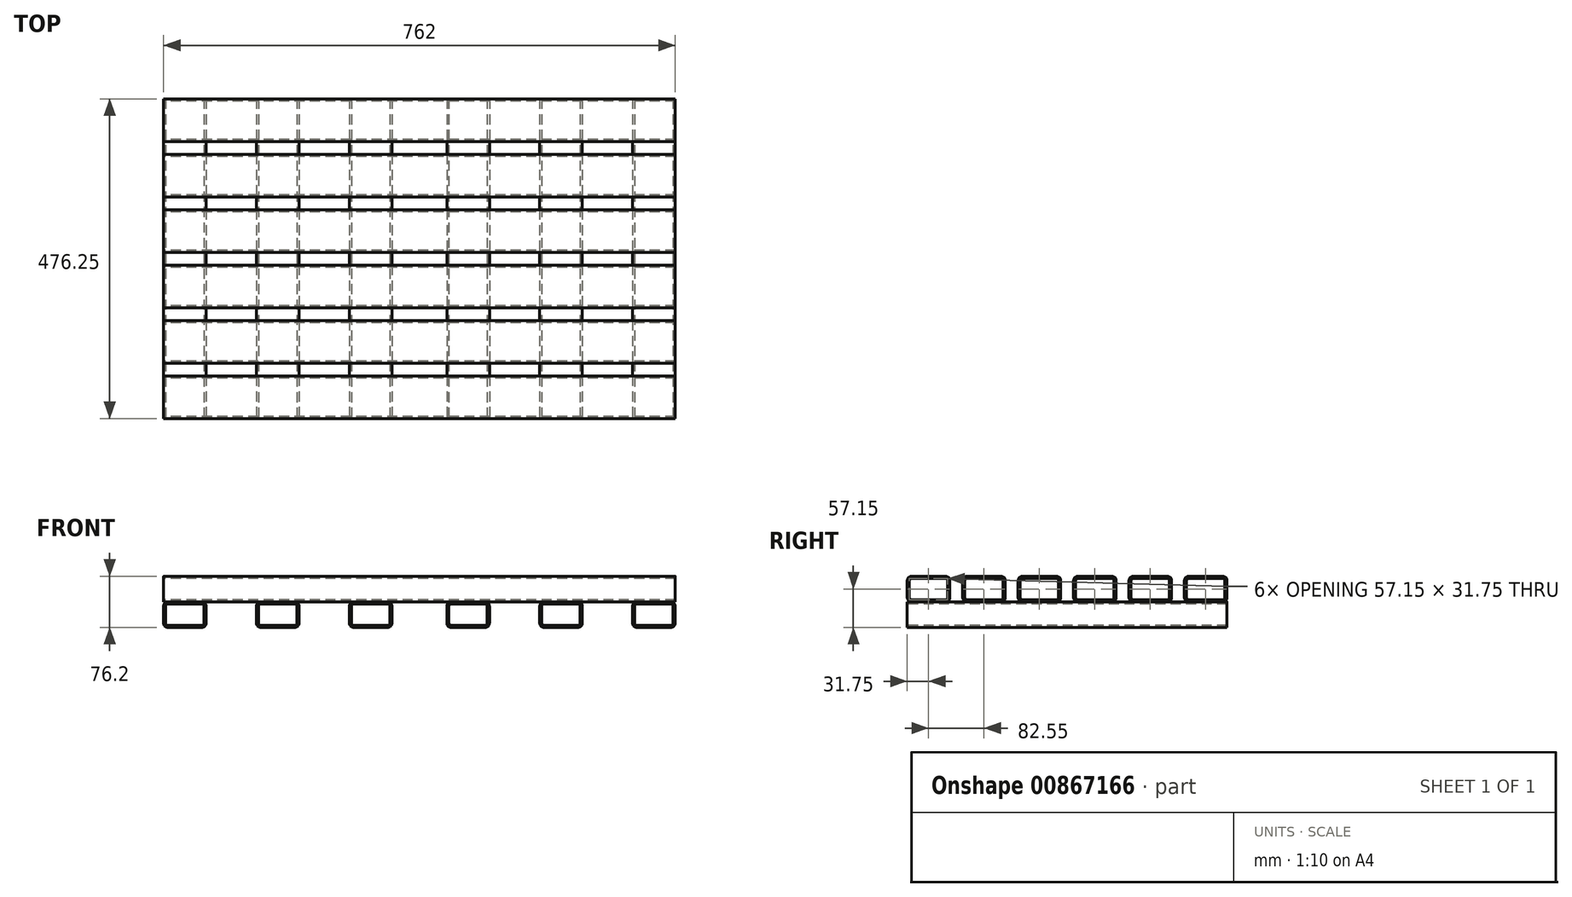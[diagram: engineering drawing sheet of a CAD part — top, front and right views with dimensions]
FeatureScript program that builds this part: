
annotation { "Feature Type Name" : "Feature", "Feature Type Description" : "" }
export const myFeature = defineFeature(function(context is Context, id is Id, definition is map)
    precondition{}
    {
        {
            var Q0;
            Q0=qCreatedBy(makeId("Right.planeOp"),FACE);
            var sketch = newSketch(context, id + "F0", { "sketchPlane" : qUnion([Q0])});
            skLineSegment(sketch, "E0.bottom", {"start": v(6.35, 0) * mm, "end": v(57.15, 0) * mm});
            skLineSegment(sketch, "E0.top", {"start": v(6.35, -38.1) * mm, "end": v(57.15, -38.1) * mm});
            skLineSegment(sketch, "E0.left", {"start": v(0, -6.35) * mm, "end": v(0, -31.75) * mm});
            skLineSegment(sketch, "E0.right", {"start": v(63.5, -6.35) * mm, "end": v(63.5, -31.75) * mm});
            skPoint(sketch, "E1.visualSharp", {"position": v(0, 0) * mm});
            skArc(sketch, "E1.filletArc", {"start": v(6.35, 0) * mm, "mid": v(1.86, -1.86) * mm, "end": v(0, -6.35) * mm});
            skPoint(sketch, "E2.visualSharp", {"position": v(0, -38.1) * mm});
            skArc(sketch, "E2.filletArc", {"start": v(0, -31.75) * mm, "mid": v(1.86, -36.24) * mm, "end": v(6.35, -38.1) * mm});
            skPoint(sketch, "E3.visualSharp", {"position": v(63.5, 0) * mm});
            skArc(sketch, "E3.filletArc", {"start": v(63.5, -6.35) * mm, "mid": v(61.64, -1.86) * mm, "end": v(57.15, 0) * mm});
            skPoint(sketch, "E4.visualSharp", {"position": v(63.5, -38.1) * mm});
            skArc(sketch, "E4.filletArc", {"start": v(57.15, -38.1) * mm, "mid": v(61.64, -36.24) * mm, "end": v(63.5, -31.75) * mm});
            skLineSegment(sketch, "E5.0", {"start": v(6.35, -3.18) * mm, "end": v(57.15, -3.18) * mm});
            skArc(sketch, "E5.1", {"start": v(60.33, -6.35) * mm, "mid": v(59.4, -4.1) * mm, "end": v(57.15, -3.17) * mm});
            skArc(sketch, "E5.2", {"start": v(6.35, -3.17) * mm, "mid": v(4.1, -4.1) * mm, "end": v(3.17, -6.35) * mm});
            skLineSegment(sketch, "E5.3", {"start": v(60.33, -6.35) * mm, "end": v(60.33, -31.75) * mm});
            skLineSegment(sketch, "E5.4", {"start": v(3.18, -6.35) * mm, "end": v(3.18, -31.75) * mm});
            skArc(sketch, "E5.5", {"start": v(3.18, -31.75) * mm, "mid": v(4.1, -34) * mm, "end": v(6.35, -34.92) * mm});
            skLineSegment(sketch, "E5.6", {"start": v(6.35, -34.92) * mm, "end": v(57.15, -34.92) * mm});
            skArc(sketch, "E5.7", {"start": v(57.15, -34.92) * mm, "mid": v(59.4, -34) * mm, "end": v(60.33, -31.75) * mm});
            skArc(sketch, "E6.1.0.0", {"start": v(88.9, 0) * mm, "mid": v(84.4, -1.86) * mm, "end": v(82.55, -6.35) * mm});
            skLineSegment(sketch, "E6.1.0.1", {"start": v(88.9, 0) * mm, "end": v(139.7, 0) * mm});
            skArc(sketch, "E6.1.0.2", {"start": v(146.05, -6.35) * mm, "mid": v(144.2, -1.86) * mm, "end": v(139.7, 0) * mm});
            skLineSegment(sketch, "E6.1.0.3", {"start": v(146.05, -6.35) * mm, "end": v(146.05, -31.75) * mm});
            skArc(sketch, "E6.1.0.4", {"start": v(139.7, -38.1) * mm, "mid": v(144.2, -36.24) * mm, "end": v(146.05, -31.75) * mm});
            skLineSegment(sketch, "E6.1.0.5", {"start": v(88.9, -38.1) * mm, "end": v(139.7, -38.1) * mm});
            skArc(sketch, "E6.1.0.6", {"start": v(82.55, -31.75) * mm, "mid": v(84.4, -36.24) * mm, "end": v(88.9, -38.1) * mm});
            skLineSegment(sketch, "E6.1.0.7", {"start": v(82.55, -6.35) * mm, "end": v(82.55, -31.75) * mm});
            skArc(sketch, "E6.1.0.8", {"start": v(88.9, -3.17) * mm, "mid": v(86.65, -4.1) * mm, "end": v(85.72, -6.35) * mm});
            skLineSegment(sketch, "E6.1.0.9", {"start": v(88.9, -3.18) * mm, "end": v(139.7, -3.18) * mm});
            skArc(sketch, "E6.1.0.10", {"start": v(142.88, -6.35) * mm, "mid": v(141.95, -4.1) * mm, "end": v(139.7, -3.17) * mm});
            skLineSegment(sketch, "E6.1.0.11", {"start": v(142.88, -6.35) * mm, "end": v(142.88, -31.75) * mm});
            skArc(sketch, "E6.1.0.12", {"start": v(139.7, -34.92) * mm, "mid": v(141.95, -34) * mm, "end": v(142.88, -31.75) * mm});
            skLineSegment(sketch, "E6.1.0.13", {"start": v(88.9, -34.92) * mm, "end": v(139.7, -34.92) * mm});
            skArc(sketch, "E6.1.0.14", {"start": v(85.73, -31.75) * mm, "mid": v(86.65, -34) * mm, "end": v(88.9, -34.92) * mm});
            skLineSegment(sketch, "E6.1.0.15", {"start": v(85.72, -6.35) * mm, "end": v(85.72, -31.75) * mm});
            skArc(sketch, "E6.2.0.0", {"start": v(171.45, 0) * mm, "mid": v(166.96, -1.86) * mm, "end": v(165.1, -6.35) * mm});
            skLineSegment(sketch, "E6.2.0.1", {"start": v(171.45, 0) * mm, "end": v(222.25, 0) * mm});
            skArc(sketch, "E6.2.0.2", {"start": v(228.6, -6.35) * mm, "mid": v(226.74, -1.86) * mm, "end": v(222.25, 0) * mm});
            skLineSegment(sketch, "E6.2.0.3", {"start": v(228.6, -6.35) * mm, "end": v(228.6, -31.75) * mm});
            skArc(sketch, "E6.2.0.4", {"start": v(222.25, -38.1) * mm, "mid": v(226.74, -36.24) * mm, "end": v(228.6, -31.75) * mm});
            skLineSegment(sketch, "E6.2.0.5", {"start": v(171.45, -38.1) * mm, "end": v(222.25, -38.1) * mm});
            skArc(sketch, "E6.2.0.6", {"start": v(165.1, -31.75) * mm, "mid": v(166.96, -36.24) * mm, "end": v(171.45, -38.1) * mm});
            skLineSegment(sketch, "E6.2.0.7", {"start": v(165.1, -6.35) * mm, "end": v(165.1, -31.75) * mm});
            skArc(sketch, "E6.2.0.8", {"start": v(171.45, -3.17) * mm, "mid": v(169.2, -4.1) * mm, "end": v(168.27, -6.35) * mm});
            skLineSegment(sketch, "E6.2.0.9", {"start": v(171.45, -3.18) * mm, "end": v(222.25, -3.18) * mm});
            skArc(sketch, "E6.2.0.10", {"start": v(225.43, -6.35) * mm, "mid": v(224.5, -4.1) * mm, "end": v(222.25, -3.17) * mm});
            skLineSegment(sketch, "E6.2.0.11", {"start": v(225.43, -6.35) * mm, "end": v(225.43, -31.75) * mm});
            skArc(sketch, "E6.2.0.12", {"start": v(222.25, -34.92) * mm, "mid": v(224.5, -34) * mm, "end": v(225.43, -31.75) * mm});
            skLineSegment(sketch, "E6.2.0.13", {"start": v(171.45, -34.92) * mm, "end": v(222.25, -34.92) * mm});
            skArc(sketch, "E6.2.0.14", {"start": v(168.27, -31.75) * mm, "mid": v(169.2, -34) * mm, "end": v(171.45, -34.92) * mm});
            skLineSegment(sketch, "E6.2.0.15", {"start": v(168.28, -6.35) * mm, "end": v(168.28, -31.75) * mm});
            skLineSegment(sketch, "E6.direction1", {"start": v(0, -6.35) * mm, "end": v(82.55, -6.35) * mm, "construction": true});
            skArc(sketch, "E7.0.3.0", {"start": v(254, 0) * mm, "mid": v(249.5, -1.86) * mm, "end": v(247.65, -6.35) * mm});
            skLineSegment(sketch, "E7.4.3.0", {"start": v(254, 0) * mm, "end": v(304.8, 0) * mm});
            skArc(sketch, "E7.7.3.0", {"start": v(311.15, -6.35) * mm, "mid": v(309.3, -1.86) * mm, "end": v(304.8, 0) * mm});
            skLineSegment(sketch, "E7.11.3.0", {"start": v(311.15, -6.35) * mm, "end": v(311.15, -31.75) * mm});
            skArc(sketch, "E7.14.3.0", {"start": v(304.8, -38.1) * mm, "mid": v(309.3, -36.24) * mm, "end": v(311.15, -31.75) * mm});
            skLineSegment(sketch, "E7.18.3.0", {"start": v(254, -38.1) * mm, "end": v(304.8, -38.1) * mm});
            skArc(sketch, "E7.21.3.0", {"start": v(247.65, -31.75) * mm, "mid": v(249.5, -36.24) * mm, "end": v(254, -38.1) * mm});
            skLineSegment(sketch, "E7.25.3.0", {"start": v(247.65, -6.35) * mm, "end": v(247.65, -31.75) * mm});
            skArc(sketch, "E7.28.3.0", {"start": v(254, -3.17) * mm, "mid": v(251.75, -4.1) * mm, "end": v(250.83, -6.35) * mm});
            skLineSegment(sketch, "E7.32.3.0", {"start": v(254, -3.18) * mm, "end": v(304.8, -3.18) * mm});
            skArc(sketch, "E7.35.3.0", {"start": v(307.97, -6.35) * mm, "mid": v(307.05, -4.1) * mm, "end": v(304.8, -3.17) * mm});
            skLineSegment(sketch, "E7.39.3.0", {"start": v(307.98, -6.35) * mm, "end": v(307.98, -31.75) * mm});
            skArc(sketch, "E7.42.3.0", {"start": v(304.8, -34.92) * mm, "mid": v(307.05, -34) * mm, "end": v(307.97, -31.75) * mm});
            skLineSegment(sketch, "E7.46.3.0", {"start": v(254, -34.92) * mm, "end": v(304.8, -34.92) * mm});
            skArc(sketch, "E7.49.3.0", {"start": v(250.83, -31.75) * mm, "mid": v(251.75, -34) * mm, "end": v(254, -34.92) * mm});
            skLineSegment(sketch, "E7.53.3.0", {"start": v(250.82, -6.35) * mm, "end": v(250.82, -31.75) * mm});
            skArc(sketch, "E8.0.4.0", {"start": v(336.55, 0) * mm, "mid": v(332.06, -1.86) * mm, "end": v(330.2, -6.35) * mm});
            skLineSegment(sketch, "E8.4.4.0", {"start": v(336.55, 0) * mm, "end": v(387.35, 0) * mm});
            skArc(sketch, "E8.7.4.0", {"start": v(393.7, -6.35) * mm, "mid": v(391.84, -1.86) * mm, "end": v(387.35, 0) * mm});
            skLineSegment(sketch, "E8.11.4.0", {"start": v(393.7, -6.35) * mm, "end": v(393.7, -31.75) * mm});
            skArc(sketch, "E8.14.4.0", {"start": v(387.35, -38.1) * mm, "mid": v(391.84, -36.24) * mm, "end": v(393.7, -31.75) * mm});
            skLineSegment(sketch, "E8.18.4.0", {"start": v(336.55, -38.1) * mm, "end": v(387.35, -38.1) * mm});
            skArc(sketch, "E8.21.4.0", {"start": v(330.2, -31.75) * mm, "mid": v(332.06, -36.24) * mm, "end": v(336.55, -38.1) * mm});
            skLineSegment(sketch, "E8.25.4.0", {"start": v(330.2, -6.35) * mm, "end": v(330.2, -31.75) * mm});
            skArc(sketch, "E8.28.4.0", {"start": v(336.55, -3.17) * mm, "mid": v(334.3, -4.1) * mm, "end": v(333.38, -6.35) * mm});
            skLineSegment(sketch, "E8.32.4.0", {"start": v(336.55, -3.18) * mm, "end": v(387.35, -3.18) * mm});
            skArc(sketch, "E8.35.4.0", {"start": v(390.52, -6.35) * mm, "mid": v(389.6, -4.1) * mm, "end": v(387.35, -3.17) * mm});
            skLineSegment(sketch, "E8.39.4.0", {"start": v(390.53, -6.35) * mm, "end": v(390.53, -31.75) * mm});
            skArc(sketch, "E8.42.4.0", {"start": v(387.35, -34.92) * mm, "mid": v(389.6, -34) * mm, "end": v(390.52, -31.75) * mm});
            skLineSegment(sketch, "E8.46.4.0", {"start": v(336.55, -34.92) * mm, "end": v(387.35, -34.92) * mm});
            skArc(sketch, "E8.49.4.0", {"start": v(333.38, -31.75) * mm, "mid": v(334.3, -34) * mm, "end": v(336.55, -34.92) * mm});
            skLineSegment(sketch, "E8.53.4.0", {"start": v(333.38, -6.35) * mm, "end": v(333.38, -31.75) * mm});
            skArc(sketch, "E8.0.5.0", {"start": v(419.1, 0) * mm, "mid": v(414.6, -1.86) * mm, "end": v(412.75, -6.35) * mm});
            skLineSegment(sketch, "E8.4.5.0", {"start": v(419.1, 0) * mm, "end": v(469.9, 0) * mm});
            skArc(sketch, "E8.7.5.0", {"start": v(476.25, -6.35) * mm, "mid": v(474.4, -1.86) * mm, "end": v(469.9, 0) * mm});
            skLineSegment(sketch, "E8.11.5.0", {"start": v(476.25, -6.35) * mm, "end": v(476.25, -31.75) * mm});
            skArc(sketch, "E8.14.5.0", {"start": v(469.9, -38.1) * mm, "mid": v(474.4, -36.24) * mm, "end": v(476.25, -31.75) * mm});
            skLineSegment(sketch, "E8.18.5.0", {"start": v(419.1, -38.1) * mm, "end": v(469.9, -38.1) * mm});
            skArc(sketch, "E8.21.5.0", {"start": v(412.75, -31.75) * mm, "mid": v(414.6, -36.24) * mm, "end": v(419.1, -38.1) * mm});
            skLineSegment(sketch, "E8.25.5.0", {"start": v(412.75, -6.35) * mm, "end": v(412.75, -31.75) * mm});
            skArc(sketch, "E8.28.5.0", {"start": v(419.1, -3.17) * mm, "mid": v(416.85, -4.1) * mm, "end": v(415.93, -6.35) * mm});
            skLineSegment(sketch, "E8.32.5.0", {"start": v(419.1, -3.18) * mm, "end": v(469.9, -3.18) * mm});
            skArc(sketch, "E8.35.5.0", {"start": v(473.07, -6.35) * mm, "mid": v(472.15, -4.1) * mm, "end": v(469.9, -3.17) * mm});
            skLineSegment(sketch, "E8.39.5.0", {"start": v(473.08, -6.35) * mm, "end": v(473.08, -31.75) * mm});
            skArc(sketch, "E8.42.5.0", {"start": v(469.9, -34.92) * mm, "mid": v(472.15, -34) * mm, "end": v(473.07, -31.75) * mm});
            skLineSegment(sketch, "E8.46.5.0", {"start": v(419.1, -34.92) * mm, "end": v(469.9, -34.92) * mm});
            skArc(sketch, "E8.49.5.0", {"start": v(415.93, -31.75) * mm, "mid": v(416.85, -34) * mm, "end": v(419.1, -34.92) * mm});
            skLineSegment(sketch, "E8.53.5.0", {"start": v(415.93, -6.35) * mm, "end": v(415.93, -31.75) * mm});
            skSolve(sketch);
        }
        {
            var Q0;
            Q0 = qSketchRegion(id + "F0", true);
            extrude(context, id + "F1", {"entities" : qUnion([Q0]), "endBound" : BoundingType.SYMMETRIC, "depth" : 762 * mm, "offsetDistance" : 25.4 * mm});
        }
        {
            var Q0;
            Q0=qCreatedBy(makeId("Front.planeOp"),FACE);
            var sketch = newSketch(context, id + "F2", { "sketchPlane" : qUnion([Q0])});
            skLineSegment(sketch, "E9.bottom", {"start": v(-236.32, -38.1) * mm, "end": v(-185.52, -38.1) * mm});
            skLineSegment(sketch, "E9.top", {"start": v(-236.32, -76.2) * mm, "end": v(-185.52, -76.2) * mm});
            skLineSegment(sketch, "E9.left", {"start": v(-242.67, -44.45) * mm, "end": v(-242.67, -69.85) * mm});
            skLineSegment(sketch, "E9.right", {"start": v(-179.17, -44.45) * mm, "end": v(-179.17, -69.85) * mm});
            skPoint(sketch, "E10.visualSharp", {"position": v(-242.67, -38.1) * mm});
            skArc(sketch, "E10.filletArc", {"start": v(-236.32, -38.1) * mm, "mid": v(-240.81, -39.96) * mm, "end": v(-242.67, -44.45) * mm});
            skPoint(sketch, "E11.visualSharp", {"position": v(-242.67, -76.2) * mm});
            skArc(sketch, "E11.filletArc", {"start": v(-242.67, -69.85) * mm, "mid": v(-240.81, -74.34) * mm, "end": v(-236.32, -76.2) * mm});
            skPoint(sketch, "E12.visualSharp", {"position": v(-179.17, -38.1) * mm});
            skArc(sketch, "E12.filletArc", {"start": v(-179.17, -44.45) * mm, "mid": v(-181.03, -39.96) * mm, "end": v(-185.52, -38.1) * mm});
            skPoint(sketch, "E13.visualSharp", {"position": v(-179.17, -76.2) * mm});
            skArc(sketch, "E13.filletArc", {"start": v(-185.52, -76.2) * mm, "mid": v(-181.03, -74.34) * mm, "end": v(-179.17, -69.85) * mm});
            skLineSegment(sketch, "E14.0", {"start": v(-236.32, -41.28) * mm, "end": v(-185.52, -41.28) * mm});
            skArc(sketch, "E14.1", {"start": v(-182.35, -44.45) * mm, "mid": v(-183.28, -42.2) * mm, "end": v(-185.52, -41.27) * mm});
            skArc(sketch, "E14.2", {"start": v(-236.32, -41.27) * mm, "mid": v(-238.57, -42.2) * mm, "end": v(-239.5, -44.45) * mm});
            skLineSegment(sketch, "E14.3", {"start": v(-182.35, -44.45) * mm, "end": v(-182.35, -69.85) * mm});
            skLineSegment(sketch, "E14.4", {"start": v(-239.5, -44.45) * mm, "end": v(-239.5, -69.85) * mm});
            skArc(sketch, "E14.5", {"start": v(-239.5, -69.85) * mm, "mid": v(-238.57, -72.1) * mm, "end": v(-236.32, -73.02) * mm});
            skLineSegment(sketch, "E14.6", {"start": v(-236.32, -73.02) * mm, "end": v(-185.52, -73.02) * mm});
            skArc(sketch, "E14.7", {"start": v(-185.52, -73.02) * mm, "mid": v(-183.28, -72.1) * mm, "end": v(-182.35, -69.85) * mm});
            skPoint(sketch, "E15", {"position": v(-210.92, -38.1) * mm});
            skLineSegment(sketch, "E16.bottom", {"start": v(185.52, -38.1) * mm, "end": v(236.32, -38.1) * mm});
            skLineSegment(sketch, "E16.top", {"start": v(185.52, -76.2) * mm, "end": v(236.32, -76.2) * mm});
            skLineSegment(sketch, "E16.left", {"start": v(179.17, -44.45) * mm, "end": v(179.17, -69.85) * mm});
            skLineSegment(sketch, "E16.right", {"start": v(242.67, -44.45) * mm, "end": v(242.67, -69.85) * mm});
            skPoint(sketch, "E17.visualSharp", {"position": v(179.17, -38.1) * mm});
            skArc(sketch, "E17.filletArc", {"start": v(185.52, -38.1) * mm, "mid": v(181.03, -39.96) * mm, "end": v(179.17, -44.45) * mm});
            skPoint(sketch, "E18.visualSharp", {"position": v(179.17, -76.2) * mm});
            skArc(sketch, "E18.filletArc", {"start": v(179.17, -69.85) * mm, "mid": v(181.03, -74.34) * mm, "end": v(185.52, -76.2) * mm});
            skPoint(sketch, "E19.visualSharp", {"position": v(242.67, -38.1) * mm});
            skArc(sketch, "E19.filletArc", {"start": v(242.67, -44.45) * mm, "mid": v(240.81, -39.96) * mm, "end": v(236.32, -38.1) * mm});
            skPoint(sketch, "E20.visualSharp", {"position": v(242.67, -76.2) * mm});
            skArc(sketch, "E20.filletArc", {"start": v(236.32, -76.2) * mm, "mid": v(240.81, -74.34) * mm, "end": v(242.67, -69.85) * mm});
            skLineSegment(sketch, "E21.0", {"start": v(185.52, -41.28) * mm, "end": v(236.32, -41.28) * mm});
            skArc(sketch, "E21.1", {"start": v(239.5, -44.45) * mm, "mid": v(238.57, -42.2) * mm, "end": v(236.32, -41.28) * mm});
            skArc(sketch, "E21.2", {"start": v(185.52, -41.28) * mm, "mid": v(183.28, -42.2) * mm, "end": v(182.35, -44.45) * mm});
            skLineSegment(sketch, "E21.3", {"start": v(239.5, -44.45) * mm, "end": v(239.5, -69.85) * mm});
            skLineSegment(sketch, "E21.4", {"start": v(182.35, -44.45) * mm, "end": v(182.35, -69.85) * mm});
            skArc(sketch, "E21.5", {"start": v(182.35, -69.85) * mm, "mid": v(183.28, -72.1) * mm, "end": v(185.52, -73.03) * mm});
            skLineSegment(sketch, "E21.6", {"start": v(185.52, -73.02) * mm, "end": v(236.32, -73.02) * mm});
            skArc(sketch, "E21.7", {"start": v(236.32, -73.03) * mm, "mid": v(238.57, -72.1) * mm, "end": v(239.5, -69.85) * mm});
            skPoint(sketch, "E22", {"position": v(210.92, -38.1) * mm});
            skLineSegment(sketch, "E23", {"start": v(-210.92, -38.1) * mm, "end": v(-210.92, 99.79) * mm, "construction": true});
            skSolve(sketch);
        }
        {
            var Q0;
            Q0=qCreatedBy(makeId("Front.planeOp"),FACE);
            var sketch = newSketch(context, id + "F3", { "sketchPlane" : qUnion([Q0])});
            skLineSegment(sketch, "E24.bottom", {"start": v(-374.65, -38.1) * mm, "end": v(-323.85, -38.1) * mm});
            skLineSegment(sketch, "E24.top", {"start": v(-374.65, -76.2) * mm, "end": v(-323.85, -76.2) * mm});
            skLineSegment(sketch, "E24.left", {"start": v(-381, -44.45) * mm, "end": v(-381, -69.85) * mm});
            skLineSegment(sketch, "E24.right", {"start": v(-317.5, -44.45) * mm, "end": v(-317.5, -69.85) * mm});
            skPoint(sketch, "E25.visualSharp", {"position": v(-381, -38.1) * mm});
            skArc(sketch, "E25.filletArc", {"start": v(-374.65, -38.1) * mm, "mid": v(-379.14, -39.96) * mm, "end": v(-381, -44.45) * mm});
            skPoint(sketch, "E26.visualSharp", {"position": v(-381, -76.2) * mm});
            skArc(sketch, "E26.filletArc", {"start": v(-381, -69.85) * mm, "mid": v(-379.14, -74.34) * mm, "end": v(-374.65, -76.2) * mm});
            skPoint(sketch, "E27.visualSharp", {"position": v(-317.5, -38.1) * mm});
            skArc(sketch, "E27.filletArc", {"start": v(-317.5, -44.45) * mm, "mid": v(-319.36, -39.96) * mm, "end": v(-323.85, -38.1) * mm});
            skPoint(sketch, "E28.visualSharp", {"position": v(-317.5, -76.2) * mm});
            skArc(sketch, "E28.filletArc", {"start": v(-323.85, -76.2) * mm, "mid": v(-319.36, -74.34) * mm, "end": v(-317.5, -69.85) * mm});
            skLineSegment(sketch, "E29.0", {"start": v(-374.65, -41.28) * mm, "end": v(-323.85, -41.28) * mm});
            skArc(sketch, "E29.1", {"start": v(-320.68, -44.45) * mm, "mid": v(-321.6, -42.2) * mm, "end": v(-323.85, -41.27) * mm});
            skArc(sketch, "E29.2", {"start": v(-374.65, -41.28) * mm, "mid": v(-376.9, -42.2) * mm, "end": v(-377.83, -44.45) * mm});
            skLineSegment(sketch, "E29.3", {"start": v(-320.68, -44.45) * mm, "end": v(-320.68, -69.85) * mm});
            skLineSegment(sketch, "E29.4", {"start": v(-377.83, -44.45) * mm, "end": v(-377.83, -69.85) * mm});
            skArc(sketch, "E29.5", {"start": v(-377.83, -69.85) * mm, "mid": v(-376.9, -72.1) * mm, "end": v(-374.65, -73.02) * mm});
            skLineSegment(sketch, "E29.6", {"start": v(-374.65, -73.02) * mm, "end": v(-323.85, -73.02) * mm});
            skArc(sketch, "E29.7", {"start": v(-323.85, -73.02) * mm, "mid": v(-321.6, -72.1) * mm, "end": v(-320.68, -69.85) * mm});
            skPoint(sketch, "E30", {"position": v(-349.25, -38.1) * mm});
            skLineSegment(sketch, "E31.bottom", {"start": v(-98, -38.1) * mm, "end": v(-47.2, -38.1) * mm});
            skLineSegment(sketch, "E31.top", {"start": v(-98, -76.2) * mm, "end": v(-47.2, -76.2) * mm});
            skLineSegment(sketch, "E31.left", {"start": v(-104.34, -44.45) * mm, "end": v(-104.34, -69.85) * mm});
            skLineSegment(sketch, "E31.right", {"start": v(-40.84, -44.45) * mm, "end": v(-40.84, -69.85) * mm});
            skPoint(sketch, "E32.visualSharp", {"position": v(-104.34, -38.1) * mm});
            skArc(sketch, "E32.filletArc", {"start": v(-98, -38.1) * mm, "mid": v(-102.48, -39.96) * mm, "end": v(-104.34, -44.45) * mm});
            skPoint(sketch, "E33.visualSharp", {"position": v(-104.34, -76.2) * mm});
            skArc(sketch, "E33.filletArc", {"start": v(-104.34, -69.85) * mm, "mid": v(-102.48, -74.34) * mm, "end": v(-98, -76.2) * mm});
            skPoint(sketch, "E34.visualSharp", {"position": v(-40.84, -38.1) * mm});
            skArc(sketch, "E34.filletArc", {"start": v(-40.84, -44.45) * mm, "mid": v(-42.7, -39.96) * mm, "end": v(-47.2, -38.1) * mm});
            skPoint(sketch, "E35.visualSharp", {"position": v(-40.84, -76.2) * mm});
            skArc(sketch, "E35.filletArc", {"start": v(-47.2, -76.2) * mm, "mid": v(-42.7, -74.34) * mm, "end": v(-40.84, -69.85) * mm});
            skLineSegment(sketch, "E36.0", {"start": v(-98, -41.28) * mm, "end": v(-47.2, -41.28) * mm});
            skArc(sketch, "E36.1", {"start": v(-44.02, -44.45) * mm, "mid": v(-44.95, -42.2) * mm, "end": v(-47.2, -41.27) * mm});
            skArc(sketch, "E36.2", {"start": v(-98, -41.28) * mm, "mid": v(-100.24, -42.2) * mm, "end": v(-101.17, -44.45) * mm});
            skLineSegment(sketch, "E36.3", {"start": v(-44.02, -44.45) * mm, "end": v(-44.02, -69.85) * mm});
            skLineSegment(sketch, "E36.4", {"start": v(-101.17, -44.45) * mm, "end": v(-101.17, -69.85) * mm});
            skArc(sketch, "E36.5", {"start": v(-101.17, -69.85) * mm, "mid": v(-100.24, -72.1) * mm, "end": v(-98, -73.03) * mm});
            skLineSegment(sketch, "E36.6", {"start": v(-98, -73.02) * mm, "end": v(-47.2, -73.02) * mm});
            skArc(sketch, "E36.7", {"start": v(-47.2, -73.02) * mm, "mid": v(-44.95, -72.1) * mm, "end": v(-44.02, -69.85) * mm});
            skPoint(sketch, "E37", {"position": v(-72.6, -38.1) * mm});
            skLineSegment(sketch, "E38.bottom", {"start": v(47.2, -38.1) * mm, "end": v(98, -38.1) * mm});
            skLineSegment(sketch, "E38.top", {"start": v(47.2, -76.2) * mm, "end": v(98, -76.2) * mm});
            skLineSegment(sketch, "E38.left", {"start": v(40.84, -44.45) * mm, "end": v(40.84, -69.85) * mm});
            skLineSegment(sketch, "E38.right", {"start": v(104.34, -44.45) * mm, "end": v(104.34, -69.85) * mm});
            skPoint(sketch, "E39.visualSharp", {"position": v(40.84, -38.1) * mm});
            skArc(sketch, "E39.filletArc", {"start": v(47.2, -38.1) * mm, "mid": v(42.7, -39.96) * mm, "end": v(40.84, -44.45) * mm});
            skPoint(sketch, "E40.visualSharp", {"position": v(40.84, -76.2) * mm});
            skArc(sketch, "E40.filletArc", {"start": v(40.84, -69.85) * mm, "mid": v(42.7, -74.34) * mm, "end": v(47.2, -76.2) * mm});
            skPoint(sketch, "E41.visualSharp", {"position": v(104.34, -38.1) * mm});
            skArc(sketch, "E41.filletArc", {"start": v(104.34, -44.45) * mm, "mid": v(102.48, -39.96) * mm, "end": v(98, -38.1) * mm});
            skPoint(sketch, "E42.visualSharp", {"position": v(104.34, -76.2) * mm});
            skArc(sketch, "E42.filletArc", {"start": v(98, -76.2) * mm, "mid": v(102.48, -74.34) * mm, "end": v(104.34, -69.85) * mm});
            skLineSegment(sketch, "E43.0", {"start": v(47.2, -41.27) * mm, "end": v(98, -41.27) * mm});
            skArc(sketch, "E43.1", {"start": v(101.17, -44.45) * mm, "mid": v(100.24, -42.2) * mm, "end": v(98, -41.27) * mm});
            skArc(sketch, "E43.2", {"start": v(47.2, -41.28) * mm, "mid": v(44.95, -42.2) * mm, "end": v(44.02, -44.45) * mm});
            skLineSegment(sketch, "E43.3", {"start": v(101.17, -44.45) * mm, "end": v(101.17, -69.85) * mm});
            skLineSegment(sketch, "E43.4", {"start": v(44.02, -44.45) * mm, "end": v(44.02, -69.85) * mm});
            skArc(sketch, "E43.5", {"start": v(44.02, -69.85) * mm, "mid": v(44.95, -72.1) * mm, "end": v(47.2, -73.03) * mm});
            skLineSegment(sketch, "E43.6", {"start": v(47.2, -73.02) * mm, "end": v(98, -73.02) * mm});
            skArc(sketch, "E43.7", {"start": v(98, -73.02) * mm, "mid": v(100.24, -72.1) * mm, "end": v(101.17, -69.85) * mm});
            skPoint(sketch, "E44", {"position": v(72.6, -38.1) * mm});
            skLineSegment(sketch, "E45.bottom", {"start": v(323.85, -38.1) * mm, "end": v(374.65, -38.1) * mm});
            skLineSegment(sketch, "E45.top", {"start": v(323.85, -76.2) * mm, "end": v(374.65, -76.2) * mm});
            skLineSegment(sketch, "E45.left", {"start": v(317.5, -44.45) * mm, "end": v(317.5, -69.85) * mm});
            skLineSegment(sketch, "E45.right", {"start": v(381, -44.45) * mm, "end": v(381, -69.85) * mm});
            skPoint(sketch, "E46.visualSharp", {"position": v(317.5, -38.1) * mm});
            skArc(sketch, "E46.filletArc", {"start": v(323.85, -38.1) * mm, "mid": v(319.36, -39.96) * mm, "end": v(317.5, -44.45) * mm});
            skPoint(sketch, "E47.visualSharp", {"position": v(317.5, -76.2) * mm});
            skArc(sketch, "E47.filletArc", {"start": v(317.5, -69.85) * mm, "mid": v(319.36, -74.34) * mm, "end": v(323.85, -76.2) * mm});
            skPoint(sketch, "E48.visualSharp", {"position": v(381, -38.1) * mm});
            skArc(sketch, "E48.filletArc", {"start": v(381, -44.45) * mm, "mid": v(379.14, -39.96) * mm, "end": v(374.65, -38.1) * mm});
            skPoint(sketch, "E49.visualSharp", {"position": v(381, -76.2) * mm});
            skArc(sketch, "E49.filletArc", {"start": v(374.65, -76.2) * mm, "mid": v(379.14, -74.34) * mm, "end": v(381, -69.85) * mm});
            skLineSegment(sketch, "E50.0", {"start": v(323.85, -41.28) * mm, "end": v(374.65, -41.28) * mm});
            skArc(sketch, "E50.1", {"start": v(377.83, -44.45) * mm, "mid": v(376.9, -42.2) * mm, "end": v(374.65, -41.28) * mm});
            skArc(sketch, "E50.2", {"start": v(323.85, -41.28) * mm, "mid": v(321.6, -42.2) * mm, "end": v(320.68, -44.45) * mm});
            skLineSegment(sketch, "E50.3", {"start": v(377.82, -44.45) * mm, "end": v(377.82, -69.85) * mm});
            skLineSegment(sketch, "E50.4", {"start": v(320.68, -44.45) * mm, "end": v(320.68, -69.85) * mm});
            skArc(sketch, "E50.5", {"start": v(320.68, -69.85) * mm, "mid": v(321.6, -72.1) * mm, "end": v(323.85, -73.03) * mm});
            skLineSegment(sketch, "E50.6", {"start": v(323.85, -73.02) * mm, "end": v(374.65, -73.02) * mm});
            skArc(sketch, "E50.7", {"start": v(374.65, -73.03) * mm, "mid": v(376.9, -72.1) * mm, "end": v(377.82, -69.85) * mm});
            skPoint(sketch, "E51", {"position": v(349.25, -38.1) * mm});
            skSolve(sketch);
        }
        {
            var Q0;
            Q0 = qSketchRegion(id + "F2", true);
            var Q1;
            Q1 = qSketchRegion(id + "F3", true);
            var Q2;
            Q2=makeQuery(id+"F1.opExtrude","SWEPT_FACE",FACE,{"disambiguationData":[OSD([sQuery(id+"F0.wireOp",EDGE,"E8.11.5.0")])]});
            extrude(context, id + "F4", {"entities" : qUnion([Q0, Q1]), "endBound" : BoundingType.UP_TO_SURFACE, "oppositeDirection" : true, "depth" : 25.4 * mm, "endBoundEntityFace" : qUnion([Q2]), "offsetDistance" : 25.4 * mm});
        }
    });
